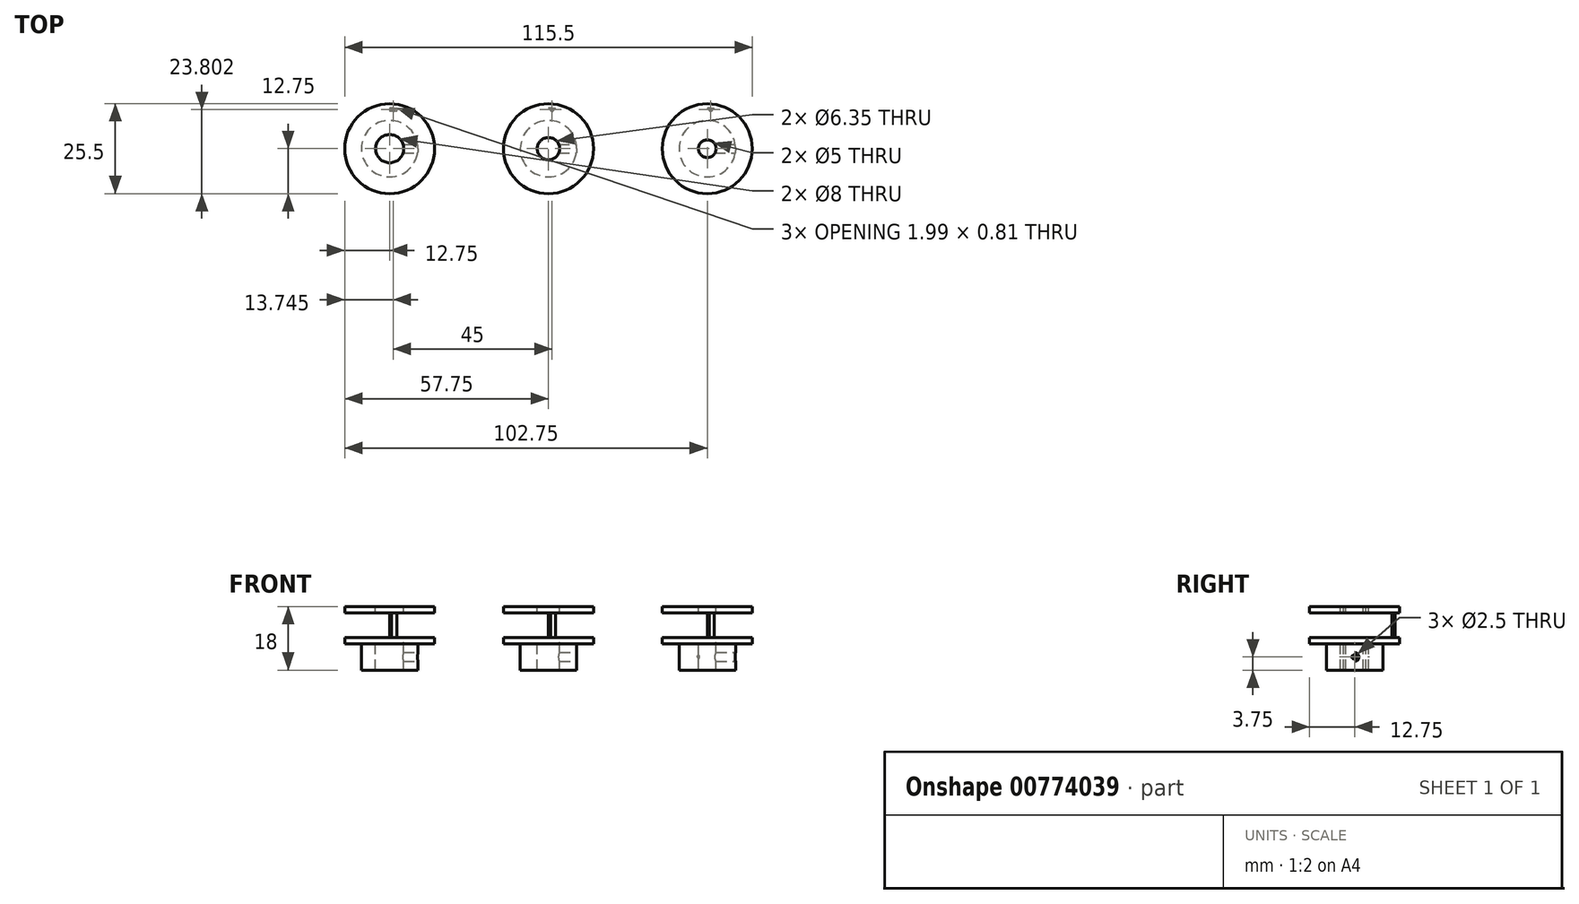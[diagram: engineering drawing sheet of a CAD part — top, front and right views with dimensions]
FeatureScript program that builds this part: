
annotation { "Feature Type Name" : "Feature", "Feature Type Description" : "" }
export const myFeature = defineFeature(function(context is Context, id is Id, definition is map)
    precondition{}
    {
        {
            var Q0;
            Q0=qCreatedBy(makeId("Front.planeOp"),FACE);
            var sketch = newSketch(context, id + "F0", { "sketchPlane" : qUnion([Q0])});
            skLineSegment(sketch, "E0", {"start": v(0, 0) * mm, "end": v(8, 0) * mm});
            skLineSegment(sketch, "E1", {"start": v(8, 0) * mm, "end": v(8, 7.5) * mm});
            skLineSegment(sketch, "E2", {"start": v(8, 7.5) * mm, "end": v(12.75, 7.5) * mm});
            skLineSegment(sketch, "E3", {"start": v(12.75, 18) * mm, "end": v(0, 18) * mm});
            skLineSegment(sketch, "E4", {"start": v(0, 18) * mm, "end": v(0, 0) * mm});
            skLineSegment(sketch, "E5", {"start": v(12.75, 16.25) * mm, "end": v(12.75, 9.25) * mm, "construction": true});
            skLineSegment(sketch, "E6", {"start": v(12.75, 16.25) * mm, "end": v(11.46, 16.25) * mm});
            skLineSegment(sketch, "E7", {"start": v(11.46, 16.25) * mm, "end": v(11.46, 9.25) * mm});
            skLineSegment(sketch, "E8", {"start": v(11.46, 9.25) * mm, "end": v(12.75, 9.25) * mm});
            skPoint(sketch, "E9", {"position": v(12.75, 12.75) * mm});
            skLineSegment(sketch, "E10", {"start": v(12.75, 18) * mm, "end": v(12.75, 16.25) * mm});
            skLineSegment(sketch, "E11", {"start": v(12.75, 9.25) * mm, "end": v(12.75, 7.5) * mm});
            skLineSegment(sketch, "E12", {"start": v(11.46, 16.25) * mm, "end": v(10.7, 16.25) * mm, "construction": true});
            skLineSegment(sketch, "E13", {"start": v(10.7, 16.25) * mm, "end": v(10.7, 9.25) * mm, "construction": true});
            skLineSegment(sketch, "E14", {"start": v(10.7, 9.25) * mm, "end": v(11.46, 9.25) * mm, "construction": true});
            skPoint(sketch, "E15", {"position": v(8, 3.5) * mm});
            skLineSegment(sketch, "E16", {"start": v(11.46, 16.25) * mm, "end": v(0, 16.25) * mm});
            skSolve(sketch);
        }
        {
            var Q0;
            {var subQ1=sQuery(id+"F0.wireOp",EDGE,"E0");Q0=makeQuery(id+"F0.imprint","IMPRINT",FACE,{"disambiguationData":[TD([[makeQuery(id+"F0.imprint","IMPRINT",EDGE,{"derivedFrom":subQ1}),1.0]])]});}
            var Q1;
            Q1=sQuery(id+"F0.wireOp",EDGE,"E4");
            revolve(context, id + "F1", {"surfaceOperationType" : NewSurfaceOperationType.NEW, "entities" : qUnion([Q0]), "axis" : qUnion([Q1]), "revolveType" : RevolveType.FULL});
        }
        {
            var Q0;
            Q0=makeQuery(id+"F1.opRevolve","SWEPT_FACE",FACE,{"disambiguationData":[OSD([sQuery(id+"F0.wireOp",EDGE,"E16")])]});
            var sketch = newSketch(context, id + "F2", { "sketchPlane" : qUnion([Q0])});
            skLineSegment(sketch, "E17", {"start": v(0, 0) * mm, "end": v(1.99, 11.29) * mm, "construction": true});
            skArc(sketch, "E18", {"start": v(1.86, 10.55) * mm, "mid": v(1.52, 10.6) * mm, "end": v(1.17, 10.64) * mm, "construction": true});
            skArc(sketch, "E19", {"start": v(0, 10.9) * mm, "mid": v(0.95, 10.86) * mm, "end": v(1.9, 10.74) * mm, "construction": true});
            skLineSegment(sketch, "E20", {"start": v(0, 0) * mm, "end": v(1, 11.42) * mm, "construction": true});
            skArc(sketch, "E21", {"start": v(0, 10.9) * mm, "mid": v(-0.95, 10.86) * mm, "end": v(-1.9, 10.74) * mm, "construction": true});
            skLineSegment(sketch, "E22", {"start": v(-1.9, 10.74) * mm, "end": v(0, 0) * mm, "construction": true});
            skArc(sketch, "E23", {"start": v(0.7, 10.69) * mm, "mid": v(0.6, 10.74) * mm, "end": v(0.55, 10.84) * mm});
            skArc(sketch, "E24", {"start": v(0, 11.46) * mm, "mid": v(0.4, 11.3) * mm, "end": v(0.55, 10.89) * mm});
            skLineSegment(sketch, "E25", {"start": v(0.55, 10.84) * mm, "end": v(0.55, 10.89) * mm});
            skLineSegment(sketch, "E26", {"start": v(0.55, 10.89) * mm, "end": v(-0.45, 10.9) * mm, "construction": true});
            skLineSegment(sketch, "E27", {"start": v(-0.45, 10.9) * mm, "end": v(0.55, 10.84) * mm, "construction": true});
            skArc(sketch, "E28.MirrorCS", {"start": v(1.17, 10.64) * mm, "mid": v(1.28, 10.68) * mm, "end": v(1.34, 10.77) * mm});
            skArc(sketch, "E29.MirrorCS", {"start": v(1.99, 11.29) * mm, "mid": v(1.57, 11.19) * mm, "end": v(1.34, 10.82) * mm});
            skLineSegment(sketch, "E30.MirrorCS", {"start": v(1.34, 10.77) * mm, "end": v(1.34, 10.82) * mm});
            skArc(sketch, "E31", {"start": v(0.7, 10.69) * mm, "mid": v(-0.59, 10.7) * mm, "end": v(-1.86, 10.55) * mm, "construction": true});
            skArc(sketch, "E32", {"start": v(1.17, 10.64) * mm, "mid": v(0.93, 10.67) * mm, "end": v(0.7, 10.69) * mm});
            skSolve(sketch);
        }
        {
            var Q0;
            Q0=makeQuery(id+"F2.imprint","IMPRINT",FACE,{"disambiguationData":[TD([[makeQuery(id+"F2.imprint","IMPRINT",EDGE,{"derivedFrom":sQuery(id+"F2.wireOp",EDGE,"E23")}),-1.0]])]});
            var Q1;
            Q1=makeQuery(id+"F1.opRevolve","SWEPT_FACE",FACE,{"disambiguationData":[OSD([sQuery(id+"F0.wireOp",EDGE,"E8")])]});
            extrude(context, id + "F3", {"entities" : qUnion([Q0]), "operationType" : NewBodyOperationType.REMOVE, "endBound" : BoundingType.UP_TO_SURFACE, "oppositeDirection" : true, "depth" : 25 * mm, "endBoundEntityFace" : qUnion([Q1]), "offsetDistance" : 25 * mm});
        }
        {
            var Q0;
            {var subQ1=sQuery(id+"F0.wireOp",EDGE,"E3");Q0=makeQuery(id+"F0.imprint","IMPRINT",FACE,{"disambiguationData":[TD([[makeQuery(id+"F0.imprint","IMPRINT",EDGE,{"derivedFrom":subQ1}),1.0]])]});}
            var Q1;
            Q1=sQuery(id+"F0.wireOp",EDGE,"E4");
            revolve(context, id + "F4", {"operationType" : NewBodyOperationType.ADD, "surfaceOperationType" : NewSurfaceOperationType.NEW, "entities" : qUnion([Q0]), "axis" : qUnion([Q1]), "revolveType" : RevolveType.FULL});
        }
        {
            var Q0;
            Q0=qCreatedBy(makeId("Right.planeOp"),FACE);
            var Q1;
            Q1=sQuery(id+"F0.wireOp",VERTEX,"E15");
            cPlane(context, id + "F5", {"entities" : qUnion([Q0, Q1]), "cplaneType" : CPlaneType.PLANE_POINT, "offset" : 25 * mm, "width" : 150 * mm, "height" : 150 * mm});
        }
        {
            var Q0;
            Q0=qCreatedBy(id+"F5.planeOp",FACE);
            var sketch = newSketch(context, id + "F6", { "sketchPlane" : qUnion([Q0])});
            skPoint(sketch, "E33.0", {"position": v(0, 3.75) * mm});
            skSolve(sketch);
        }
        {
            var Q0;
            Q0=sQuery(id+"F6.wireOp",VERTEX,"E33.0");
            var Q1;
            Q1=makeQuery(id+"F1.opRevolve","SWEPT_BODY",BODY,{"disambiguationData":[OSD([sQuery(id+"F0.wireOp",EDGE,"E0"),sQuery(id+"F0.wireOp",EDGE,"E1"),sQuery(id+"F0.wireOp",EDGE,"E2"),sQuery(id+"F0.wireOp",EDGE,"E4"),sQuery(id+"F0.wireOp",EDGE,"E7"),sQuery(id+"F0.wireOp",EDGE,"E8"),sQuery(id+"F0.wireOp",EDGE,"E11"),sQuery(id+"F0.wireOp",EDGE,"E16")])]});
            hole(context, id + "F7", {"style" : HoleStyle.SIMPLE, "endStyle" : HoleEndStyle.BLIND, "standardTappedOrClearance" : lookupTablePath({ "standard" : "ISO", "engagement" : "75%", "pitch" : "0.5 mm", "size" : "M3", "type" : "Tapped" }), "standardBlindInLast" : lookupTablePath({ "standard" : "ISO", "engagement" : "75%", "pitch" : "0.5 mm", "size" : "M3", "type" : "Tapped" }), "holeDiameter" : 2.5 * mm, "majorDiameter" : 3 * mm, "showTappedDepth" : true, "holeDepth" : 10 * mm, "isTappedThrough" : true, "tappedDepth" : 8.5 * mm, "tapClearance" : 3, "locations" : qUnion([Q0]), "scope" : qUnion([Q1])});
        }
        {
            var Q0;
            Q0=makeQuery(id+"F1.opRevolve","SWEPT_BODY",BODY,{"disambiguationData":[OSD([sQuery(id+"F0.wireOp",EDGE,"E0"),sQuery(id+"F0.wireOp",EDGE,"E1"),sQuery(id+"F0.wireOp",EDGE,"E2"),sQuery(id+"F0.wireOp",EDGE,"E4"),sQuery(id+"F0.wireOp",EDGE,"E7"),sQuery(id+"F0.wireOp",EDGE,"E8"),sQuery(id+"F0.wireOp",EDGE,"E11"),sQuery(id+"F0.wireOp",EDGE,"E16")])]});
            transform(context, id + "F8", {"entities" : qUnion([Q0]), "transformType" : TransformType.TRANSLATION_3D, "dx" : 45 * mm, "dy" : 0 * mm, "dz" : 0 * mm, "makeCopy" : true});
        }
        {
            var Q0;
            Q0=makeQuery(id+"F8.opPattern","COPY",BODY,{"derivedFrom":makeQuery(id+"F1.opRevolve","SWEPT_BODY",BODY,{"disambiguationData":[OSD([sQuery(id+"F0.wireOp",EDGE,"E0"),sQuery(id+"F0.wireOp",EDGE,"E1"),sQuery(id+"F0.wireOp",EDGE,"E2"),sQuery(id+"F0.wireOp",EDGE,"E4"),sQuery(id+"F0.wireOp",EDGE,"E7"),sQuery(id+"F0.wireOp",EDGE,"E8"),sQuery(id+"F0.wireOp",EDGE,"E11"),sQuery(id+"F0.wireOp",EDGE,"E16")])]}),"instanceName":"1"});
            transform(context, id + "F9", {"entities" : qUnion([Q0]), "transformType" : TransformType.TRANSLATION_3D, "dx" : 45 * mm, "dy" : 0 * mm, "dz" : 0 * mm, "makeCopy" : true});
        }
        {
            var Q0;
            Q0=makeQuery(id+"F4.opRevolve","SWEPT_FACE",FACE,{"disambiguationData":[OSD([sQuery(id+"F0.wireOp",EDGE,"E3")])]});
            var sketch = newSketch(context, id + "F10", { "sketchPlane" : qUnion([Q0])});
            skPoint(sketch, "E34", {"position": v(0, 0) * mm});
            skPoint(sketch, "E35", {"position": v(45, 0) * mm});
            skPoint(sketch, "E36", {"position": v(90, 0) * mm});
            skSolve(sketch);
        }
        {
            var Q0;
            Q0=sQuery(id+"F10.wireOp",VERTEX,"E34");
            var Q1;
            Q1=makeQuery(id+"F1.opRevolve","SWEPT_BODY",BODY,{"disambiguationData":[OSD([sQuery(id+"F0.wireOp",EDGE,"E0"),sQuery(id+"F0.wireOp",EDGE,"E1"),sQuery(id+"F0.wireOp",EDGE,"E2"),sQuery(id+"F0.wireOp",EDGE,"E4"),sQuery(id+"F0.wireOp",EDGE,"E7"),sQuery(id+"F0.wireOp",EDGE,"E8"),sQuery(id+"F0.wireOp",EDGE,"E11"),sQuery(id+"F0.wireOp",EDGE,"E16")])]});
            hole(context, id + "F11", {"style" : HoleStyle.SIMPLE, "endStyle" : HoleEndStyle.THROUGH, "holeDiameter" : 8 * mm, "majorDiameter" : 8 * mm, "isTappedThrough" : true, "tappedDepth" : 8.5 * mm, "tapClearance" : 3, "locations" : qUnion([Q0]), "scope" : qUnion([Q1])});
        }
        {
            var Q0;
            Q0=sQuery(id+"F10.wireOp",VERTEX,"E35");
            var Q1;
            Q1=makeQuery(id+"F8.opPattern","COPY",BODY,{"derivedFrom":makeQuery(id+"F1.opRevolve","SWEPT_BODY",BODY,{"disambiguationData":[OSD([sQuery(id+"F0.wireOp",EDGE,"E0"),sQuery(id+"F0.wireOp",EDGE,"E1"),sQuery(id+"F0.wireOp",EDGE,"E2"),sQuery(id+"F0.wireOp",EDGE,"E4"),sQuery(id+"F0.wireOp",EDGE,"E7"),sQuery(id+"F0.wireOp",EDGE,"E8"),sQuery(id+"F0.wireOp",EDGE,"E11"),sQuery(id+"F0.wireOp",EDGE,"E16")])]}),"instanceName":"1"});
            hole(context, id + "F12", {"style" : HoleStyle.SIMPLE, "endStyle" : HoleEndStyle.THROUGH, "holeDiameter" : 6.35 * mm, "majorDiameter" : 5 * mm, "isTappedThrough" : true, "tappedDepth" : 8.5 * mm, "tapClearance" : 3, "locations" : qUnion([Q0]), "scope" : qUnion([Q1])});
        }
        {
            var Q0;
            Q0=sQuery(id+"F10.wireOp",VERTEX,"E36");
            var Q1;
            Q1=makeQuery(id+"F9.opPattern","COPY",BODY,{"derivedFrom":makeQuery(id+"F8.opPattern","COPY",BODY,{"derivedFrom":makeQuery(id+"F1.opRevolve","SWEPT_BODY",BODY,{"disambiguationData":[OSD([sQuery(id+"F0.wireOp",EDGE,"E0"),sQuery(id+"F0.wireOp",EDGE,"E1"),sQuery(id+"F0.wireOp",EDGE,"E2"),sQuery(id+"F0.wireOp",EDGE,"E4"),sQuery(id+"F0.wireOp",EDGE,"E7"),sQuery(id+"F0.wireOp",EDGE,"E8"),sQuery(id+"F0.wireOp",EDGE,"E11"),sQuery(id+"F0.wireOp",EDGE,"E16")])]}),"instanceName":"1"}),"instanceName":"1"});
            hole(context, id + "F13", {"style" : HoleStyle.SIMPLE, "endStyle" : HoleEndStyle.THROUGH, "holeDiameter" : 5 * mm, "majorDiameter" : 5 * mm, "isTappedThrough" : true, "tappedDepth" : 8.5 * mm, "tapClearance" : 3, "locations" : qUnion([Q0]), "scope" : qUnion([Q1])});
        }
    });
